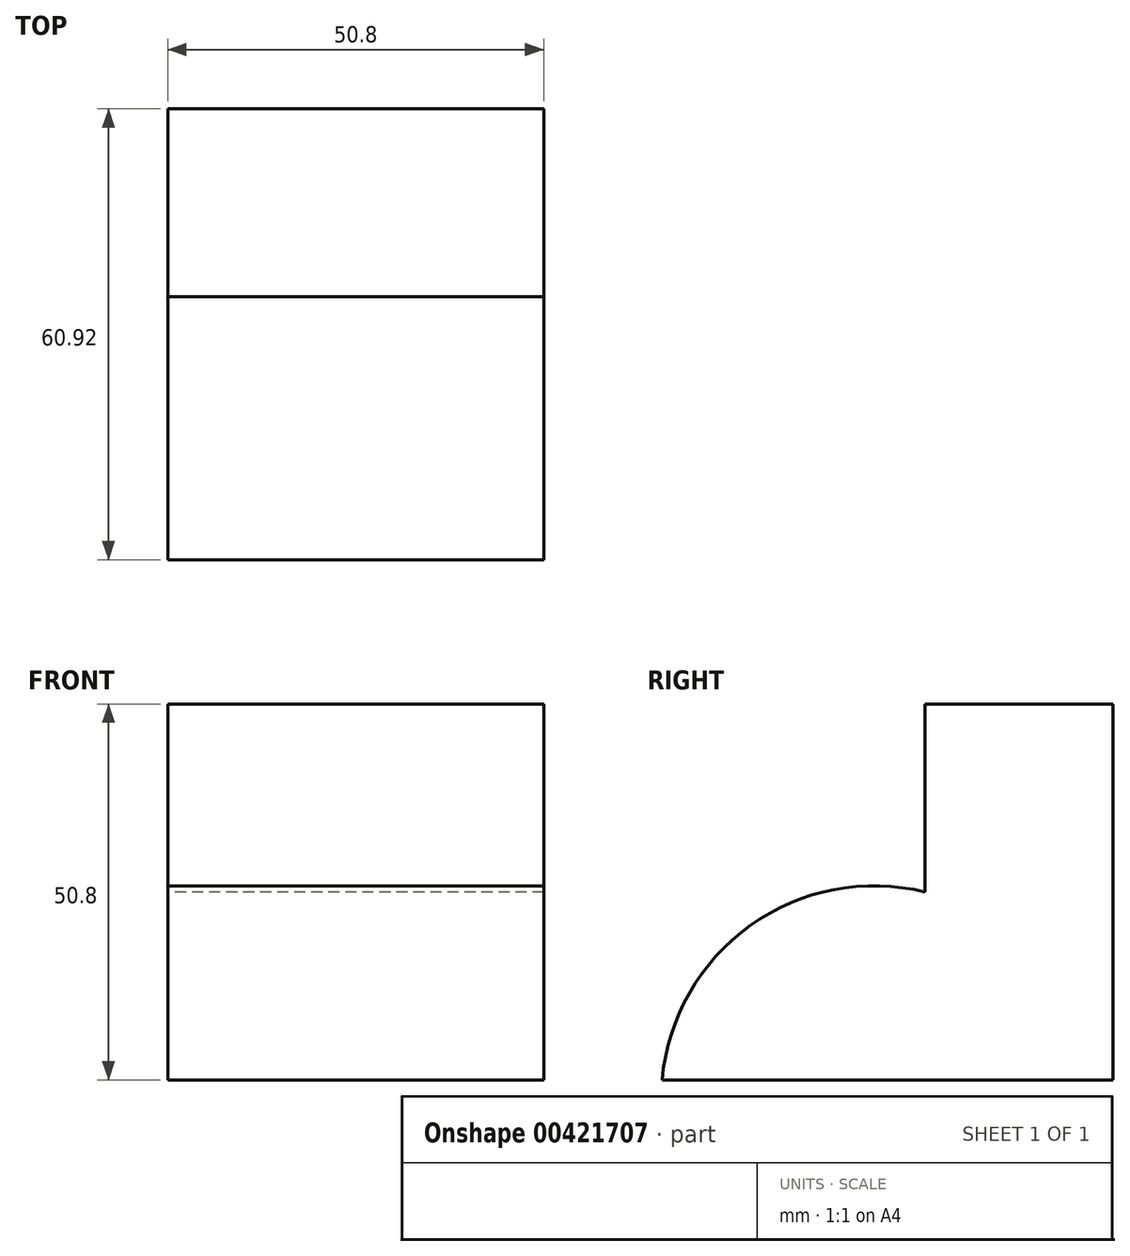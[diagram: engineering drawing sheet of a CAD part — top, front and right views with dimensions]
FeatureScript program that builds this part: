
annotation { "Feature Type Name" : "Feature", "Feature Type Description" : "" }
export const myFeature = defineFeature(function(context is Context, id is Id, definition is map)
    precondition{}
    {
        {
            var Q0;
            Q0=qCreatedBy(makeId("Front.planeOp"),FACE);
            var sketch = newSketch(context, id + "F0", { "sketchPlane" : qUnion([Q0])});
            skLineSegment(sketch, "E0.bottom", {"start": v(0, 0) * mm, "end": v(50.8, 0) * mm});
            skLineSegment(sketch, "E0.top", {"start": v(0, 50.8) * mm, "end": v(50.8, 50.8) * mm});
            skLineSegment(sketch, "E0.left", {"start": v(0, 0) * mm, "end": v(0, 50.8) * mm});
            skLineSegment(sketch, "E0.right", {"start": v(50.8, 0) * mm, "end": v(50.8, 50.8) * mm});
            skSolve(sketch);
        }
        {
            var Q0;
            Q0=makeQuery(id+"F0.imprint","IMPRINT",FACE,{"disambiguationData":[TD([[makeQuery(id+"F0.imprint","IMPRINT",EDGE,{"derivedFrom":sQuery(id+"F0.wireOp",EDGE,"E0.bottom")}),1.0]])]});
            extrude(context, id + "F1", {"entities" : qUnion([Q0]), "depth" : 25.4 * mm});
        }
        {
            var Q0;
            Q0=makeQuery(id+"F1.opExtrude","SWEPT_FACE",FACE,{"disambiguationData":[OSD([sQuery(id+"F0.wireOp",EDGE,"E0.left")])]});
            var sketch = newSketch(context, id + "F2", { "sketchPlane" : qUnion([Q0])});
            skArc(sketch, "E1", {"start": v(60.92, 0) * mm, "mid": v(49, 20.85) * mm, "end": v(25.4, 25.4) * mm});
            skLineSegment(sketch, "E2", {"start": v(25.4, 0) * mm, "end": v(60.92, 0) * mm});
            skSolve(sketch);
        }
        {
            var Q0;
            {var subQ0=sQuery(id+"F2.wireOp",EDGE,"E1");Q0=makeQuery(id+"F2.imprint","IMPRINT",FACE,{"disambiguationData":[TD([[makeQuery(id+"F2.imprint","IMPRINT",EDGE,{"derivedFrom":subQ0}),1.0]])]});}
            extrude(context, id + "F3", {"entities" : qUnion([Q0]), "operationType" : NewBodyOperationType.ADD, "oppositeDirection" : true, "depth" : 50.8 * mm});
        }
    });
